# Revit family: Bed_Hotel
name_source: partatom
category: Furniture
units: mm (PartAtom-declared; Revit-internal decimal feet)

## family parameters
Always vertical = Yes
Classification Number = 23.40.70.14.21
Cut with Voids When Loaded = No
Enable Cutting in Views = No
Render Appearance Source = Family Geometry
Room Calculation Point = No
Shared = No
Work Plane-Based = No

## types (4) — shared parameters
Assembly Code = E2020200
Construction Details = http://www.arcat.com
Default Elevation = 0' - 0"
Depth = 0' - 10"
Expected Lifespan (Years) = 10
Flammability = CPSC - 16CFR - Part 1633 Approved
Frame Material = ARCAT - Wood - Cherry
Green Building - LEED = http://www.arcat.com
Height from ground = 1' - 0"
Keynote = 12450
Maintenance Schedule (Months) = 6
Manufacturer = Generic
Manufacturer Fax = (203) 929-9444
Manufacturer Website = http://www.arcat.com
Model = Generic
Product Data = http://www.arcat.com
Product Properties = http://www.arcat.com
Rigidity = Firm
Specification = http://www.arcat.com
Textiles = ARCAT - Fabric - Generic
Warranty Duration (Years) = 10

## per-type parameters (varying)
| type | Description | Length | Sleeping Capacity | Width |
| Twin | Hotel Bed - Twin | 6' - 3" | 1 | 3' - 3" |
| Full_Double | Hotel Bed - Full/Double | 6' - 3" | 2 | 4' - 6" |
| Queen | Hotel Bed - Queen | 6' - 8" | 2 | 5' - 0" |
| King | Hotel Bed - King | 6' - 8" | 2 | 6' - 4" |

## geometry (parser evidence)
native form markers: Sweep x3
no freeform markers — native parametric forms only
